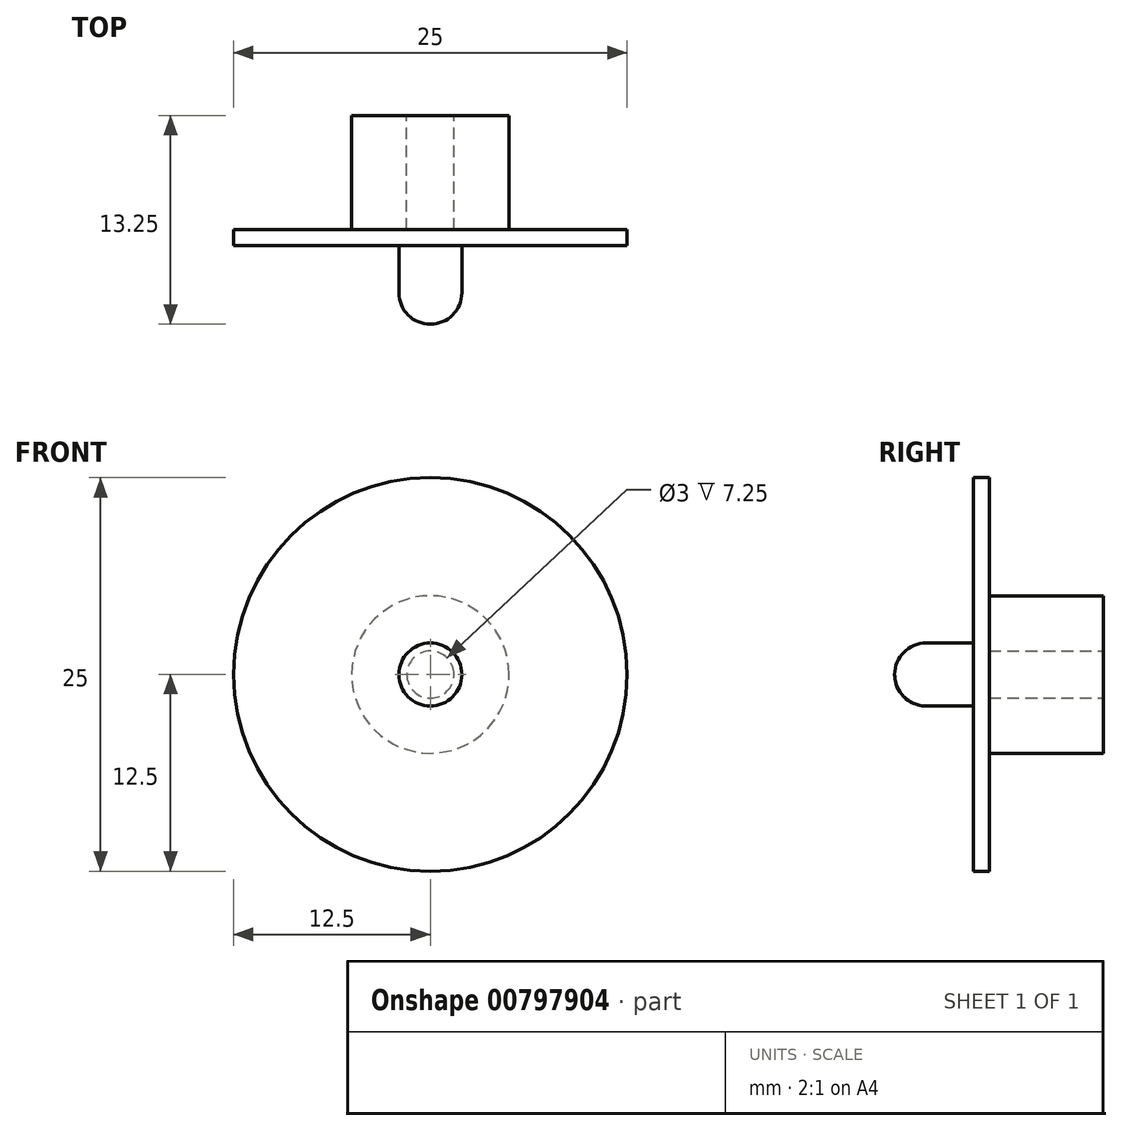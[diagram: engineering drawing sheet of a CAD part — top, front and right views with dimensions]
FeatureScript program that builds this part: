
annotation { "Feature Type Name" : "Feature", "Feature Type Description" : "" }
export const myFeature = defineFeature(function(context is Context, id is Id, definition is map)
    precondition{}
    {
        {
            var Q0;
            Q0=qCreatedBy(makeId("Front.planeOp"),FACE);
            var sketch = newSketch(context, id + "F0", { "sketchPlane" : qUnion([Q0])});
            skCircle(sketch, "E0", {"center": v(0, 0) * mm, "radius": 1.5 * mm});
            skCircle(sketch, "E1", {"center": v(0, 0) * mm, "radius": 5 * mm});
            skSolve(sketch);
        }
        {
            var Q0;
            Q0 = qSketchRegion(id + "F0", true);
            extrude(context, id + "F1", {"entities" : qUnion([Q0]), "depth" : 7.25 * mm, "offsetDistance" : 25 * mm});
        }
        {
            var Q0;
            Q0=makeQuery(id+"F1.opExtrude","CAP_FACE",FACE,{"disambiguationData":[OSD([sQuery(id+"F0.wireOp",EDGE,"E0"),sQuery(id+"F0.wireOp",EDGE,"E1")])],"isStart":false});
            var sketch = newSketch(context, id + "F2", { "sketchPlane" : qUnion([Q0])});
            skCircle(sketch, "E2", {"center": v(0, 0) * mm, "radius": 12.5 * mm});
            skSolve(sketch);
        }
        {
            var Q0;
            Q0 = qSketchRegion(id + "F2", true);
            extrude(context, id + "F3", {"entities" : qUnion([Q0]), "operationType" : NewBodyOperationType.ADD, "depth" : 1 * mm, "offsetDistance" : 25 * mm});
        }
        {
            var Q0;
            Q0=makeQuery(id+"F3.opExtrude","CAP_FACE",FACE,{"disambiguationData":[OSD([sQuery(id+"F2.wireOp",EDGE,"E2")])],"isStart":false});
            var sketch = newSketch(context, id + "F4", { "sketchPlane" : qUnion([Q0])});
            skCircle(sketch, "E3", {"center": v(0, 0) * mm, "radius": 2 * mm});
            skSolve(sketch);
        }
        {
            var Q0;
            Q0 = qSketchRegion(id + "F4", true);
            extrude(context, id + "F5", {"entities" : qUnion([Q0]), "operationType" : NewBodyOperationType.ADD, "depth" : 5 * mm, "offsetDistance" : 25 * mm});
        }
        {
            var Q0;
            Q0=makeQuery(id+"F5.opExtrude","CAP_EDGE",EDGE,{"disambiguationData":[OSD([sQuery(id+"F4.wireOp",EDGE,"E3")])],"isStart":false});
            fillet(context, id + "F6", {"entities" : qUnion([Q0]), "radius" : 2 * mm, "tangentPropagation" : true, "allowEdgeOverflow" : false});
        }
    });
